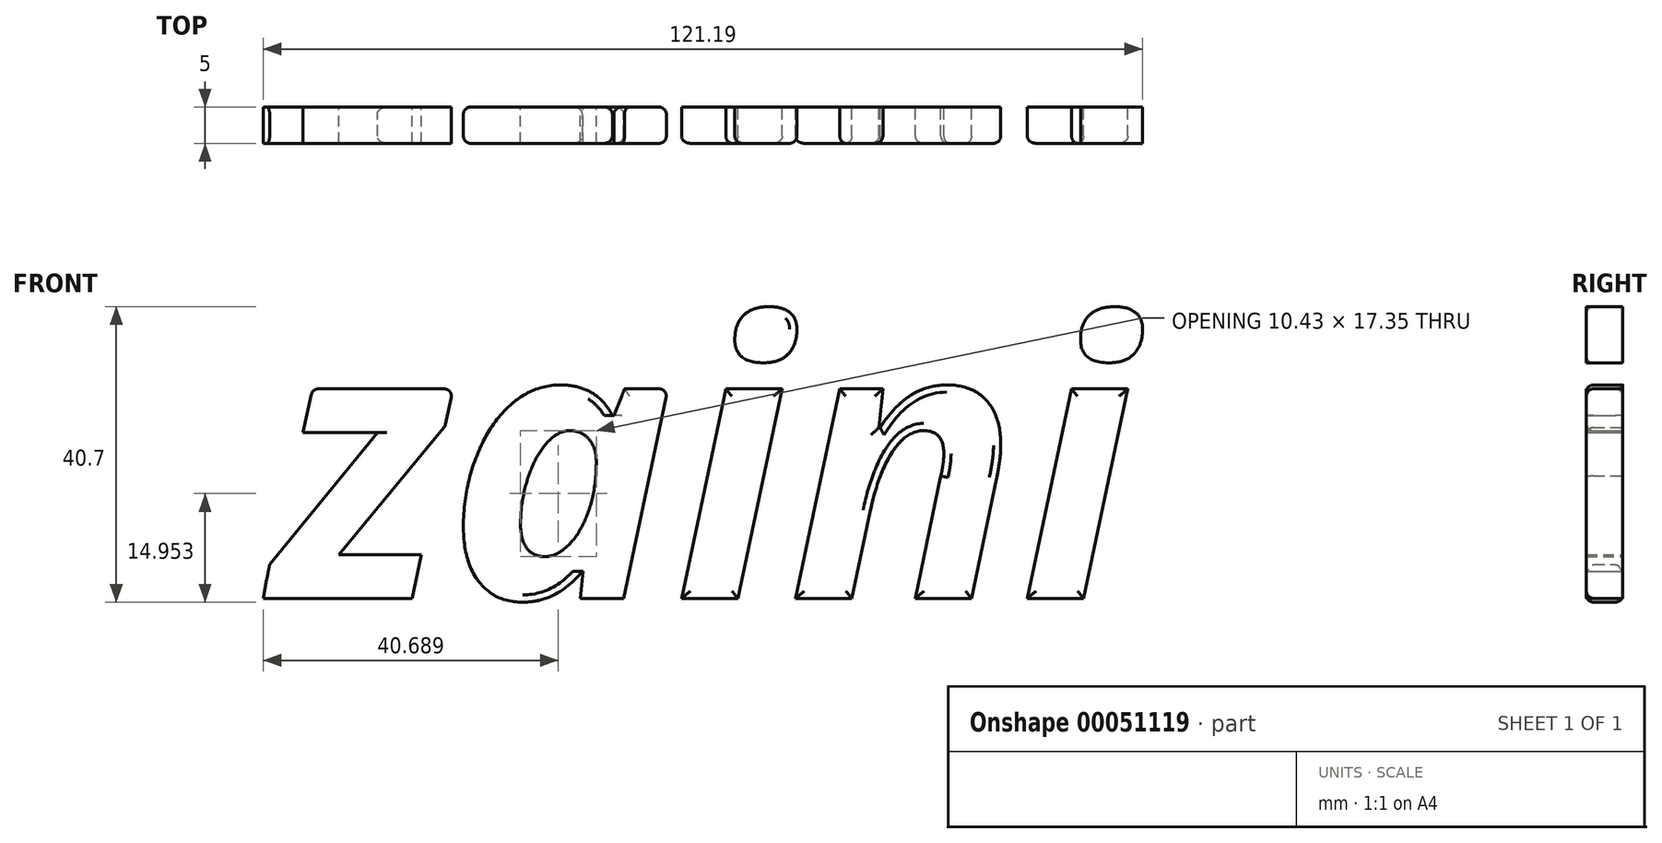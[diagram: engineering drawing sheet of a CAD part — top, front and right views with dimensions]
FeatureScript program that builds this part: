
annotation { "Feature Type Name" : "Feature", "Feature Type Description" : "" }
export const myFeature = defineFeature(function(context is Context, id is Id, definition is map)
    precondition{}
    {
        {
            var Q0;
            Q0=qCreatedBy(makeId("Front.planeOp"),FACE);
            var sketch = newSketch(context, id + "F0", { "sketchPlane" : qUnion([Q0])});
            skText(sketch, "E0", { "text": "zaini", "fontName": "OpenSans-BoldItalic.ttf"});
            const initialGuessF0  = {"E0": [0, 0.04462, 1, 0, 0.03807]};
            skSetInitialGuess(sketch, initialGuessF0);
            skSolve(sketch);
        }
        {
            var Q0;
            Q0 = qSketchRegion(id + "F0", true);
            extrude(context, id + "F1", {"entities" : qUnion([Q0]), "depth" : 5 * mm});
        }
        {
            var Q0;
            Q0=makeQuery(id+"F1.opExtrude","SWEPT_EDGE",EDGE,{"disambiguationData":[OSD([sQuery(id+"F0.wireOp",EDGE,"E0.sketch_text.stroke-5"),sQuery(id+"F0.wireOp",EDGE,"E0.sketch_text.stroke-6")])]});
            var Q1;
            Q1=makeQuery(id+"F1.opExtrude","SWEPT_EDGE",EDGE,{"disambiguationData":[OSD([sQuery(id+"F0.wireOp",EDGE,"E0.sketch_text.stroke-6"),sQuery(id+"F0.wireOp",EDGE,"E0.sketch_text.stroke-7")])]});
            var Q2;
            Q2=makeQuery(id+"F1.opExtrude","CAP_EDGE",EDGE,{"disambiguationData":[OSD([sQuery(id+"F0.wireOp",EDGE,"E0.sketch_text.stroke-2")])],"isStart":true});
            var Q3;
            Q3=makeQuery(id+"F1.opExtrude","CAP_EDGE",EDGE,{"disambiguationData":[OSD([sQuery(id+"F0.wireOp",EDGE,"E0.sketch_text.stroke-2")])],"isStart":false});
            var Q4;
            Q4=makeQuery(id+"F1.opExtrude","SWEPT_EDGE",EDGE,{"disambiguationData":[OSD([sQuery(id+"F0.wireOp",EDGE,"E0.sketch_text.stroke-4"),sQuery(id+"F0.wireOp",EDGE,"E0.sketch_text.stroke-5")])]});
            var Q5;
            Q5=makeQuery(id+"F1.opExtrude","SWEPT_EDGE",EDGE,{"disambiguationData":[OSD([sQuery(id+"F0.wireOp",EDGE,"E0.sketch_text.stroke-19"),sQuery(id+"F0.wireOp",EDGE,"E0.sketch_text.stroke-20")])]});
            var Q6;
            Q6=makeQuery(id+"F1.opExtrude","CAP_EDGE",EDGE,{"disambiguationData":[OSD([sQuery(id+"F0.wireOp",EDGE,"E0.sketch_text.stroke-20")])],"isStart":true});
            var Q7;
            Q7=makeQuery(id+"F1.opExtrude","CAP_EDGE",EDGE,{"disambiguationData":[OSD([sQuery(id+"F0.wireOp",EDGE,"E0.sketch_text.stroke-20")])],"isStart":false});
            var Q8;
            Q8=makeQuery(id+"F1.opExtrude","CAP_EDGE",EDGE,{"disambiguationData":[OSD([sQuery(id+"F0.wireOp",EDGE,"E0.sketch_text.stroke-19")])],"isStart":false});
            var Q9;
            Q9=makeQuery(id+"F1.opExtrude","CAP_EDGE",EDGE,{"disambiguationData":[OSD([sQuery(id+"F0.wireOp",EDGE,"E0.sketch_text.stroke-19")])],"isStart":true});
            var Q10;
            Q10=makeQuery(id+"F1.opExtrude","CAP_EDGE",EDGE,{"disambiguationData":[OSD([sQuery(id+"F0.wireOp",EDGE,"E0.sketch_text.stroke-18")])],"isStart":true});
            var Q11;
            Q11=makeQuery(id+"F1.opExtrude","CAP_EDGE",EDGE,{"disambiguationData":[OSD([sQuery(id+"F0.wireOp",EDGE,"E0.sketch_text.stroke-15")])],"isStart":true});
            var Q12;
            Q12=makeQuery(id+"F1.opExtrude","CAP_EDGE",EDGE,{"disambiguationData":[OSD([sQuery(id+"F0.wireOp",EDGE,"E0.sketch_text.stroke-15")])],"isStart":false});
            var Q13;
            Q13=makeQuery(id+"F1.opExtrude","CAP_FACE",FACE,{"disambiguationData":[OSD([sQuery(id+"F0.wireOp",EDGE,"E0.sketch_text.stroke-42"),sQuery(id+"F0.wireOp",EDGE,"E0.sketch_text.stroke-43"),sQuery(id+"F0.wireOp",EDGE,"E0.sketch_text.stroke-44"),sQuery(id+"F0.wireOp",EDGE,"E0.sketch_text.stroke-45")])],"isStart":false});
            var Q14;
            Q14=makeQuery(id+"F1.opExtrude","CAP_FACE",FACE,{"disambiguationData":[OSD([sQuery(id+"F0.wireOp",EDGE,"E0.sketch_text.stroke-46"),sQuery(id+"F0.wireOp",EDGE,"E0.sketch_text.stroke-47"),sQuery(id+"F0.wireOp",EDGE,"E0.sketch_text.stroke-48"),sQuery(id+"F0.wireOp",EDGE,"E0.sketch_text.stroke-49"),sQuery(id+"F0.wireOp",EDGE,"E0.sketch_text.stroke-50"),sQuery(id+"F0.wireOp",EDGE,"E0.sketch_text.stroke-51"),sQuery(id+"F0.wireOp",EDGE,"E0.sketch_text.stroke-52"),sQuery(id+"F0.wireOp",EDGE,"E0.sketch_text.stroke-53"),sQuery(id+"F0.wireOp",EDGE,"E0.sketch_text.stroke-54"),sQuery(id+"F0.wireOp",EDGE,"E0.sketch_text.stroke-55"),sQuery(id+"F0.wireOp",EDGE,"E0.sketch_text.stroke-56"),sQuery(id+"F0.wireOp",EDGE,"E0.sketch_text.stroke-57"),sQuery(id+"F0.wireOp",EDGE,"E0.sketch_text.stroke-58"),sQuery(id+"F0.wireOp",EDGE,"E0.sketch_text.stroke-59"),sQuery(id+"F0.wireOp",EDGE,"E0.sketch_text.stroke-60"),sQuery(id+"F0.wireOp",EDGE,"E0.sketch_text.stroke-61"),sQuery(id+"F0.wireOp",EDGE,"E0.sketch_text.stroke-62")])],"isStart":false});
            var Q15;
            Q15=makeQuery(id+"F1.opExtrude","CAP_FACE",FACE,{"disambiguationData":[OSD([sQuery(id+"F0.wireOp",EDGE,"E0.sketch_text.stroke-35"),sQuery(id+"F0.wireOp",EDGE,"E0.sketch_text.stroke-36"),sQuery(id+"F0.wireOp",EDGE,"E0.sketch_text.stroke-37"),sQuery(id+"F0.wireOp",EDGE,"E0.sketch_text.stroke-38"),sQuery(id+"F0.wireOp",EDGE,"E0.sketch_text.stroke-39"),sQuery(id+"F0.wireOp",EDGE,"E0.sketch_text.stroke-40"),sQuery(id+"F0.wireOp",EDGE,"E0.sketch_text.stroke-41")])],"isStart":false});
            var Q16;
            Q16=makeQuery(id+"F1.opExtrude","CAP_FACE",FACE,{"disambiguationData":[OSD([sQuery(id+"F0.wireOp",EDGE,"E0.sketch_text.stroke-70"),sQuery(id+"F0.wireOp",EDGE,"E0.sketch_text.stroke-71"),sQuery(id+"F0.wireOp",EDGE,"E0.sketch_text.stroke-72"),sQuery(id+"F0.wireOp",EDGE,"E0.sketch_text.stroke-73")])],"isStart":false});
            var Q17;
            Q17=makeQuery(id+"F1.opExtrude","CAP_FACE",FACE,{"disambiguationData":[OSD([sQuery(id+"F0.wireOp",EDGE,"E0.sketch_text.stroke-70"),sQuery(id+"F0.wireOp",EDGE,"E0.sketch_text.stroke-71"),sQuery(id+"F0.wireOp",EDGE,"E0.sketch_text.stroke-72"),sQuery(id+"F0.wireOp",EDGE,"E0.sketch_text.stroke-73")])],"isStart":false});
            fillet(context, id + "F2", {"entities" : qUnion([Q0, Q1, Q2, Q3, Q4, Q5, Q6, Q7, Q8, Q9, Q10, Q11, Q12, Q13, Q14, Q15, Q16, Q17]), "radius" : 1 * mm, "tangentPropagation" : true, "allowEdgeOverflow" : false});
        }
    });
